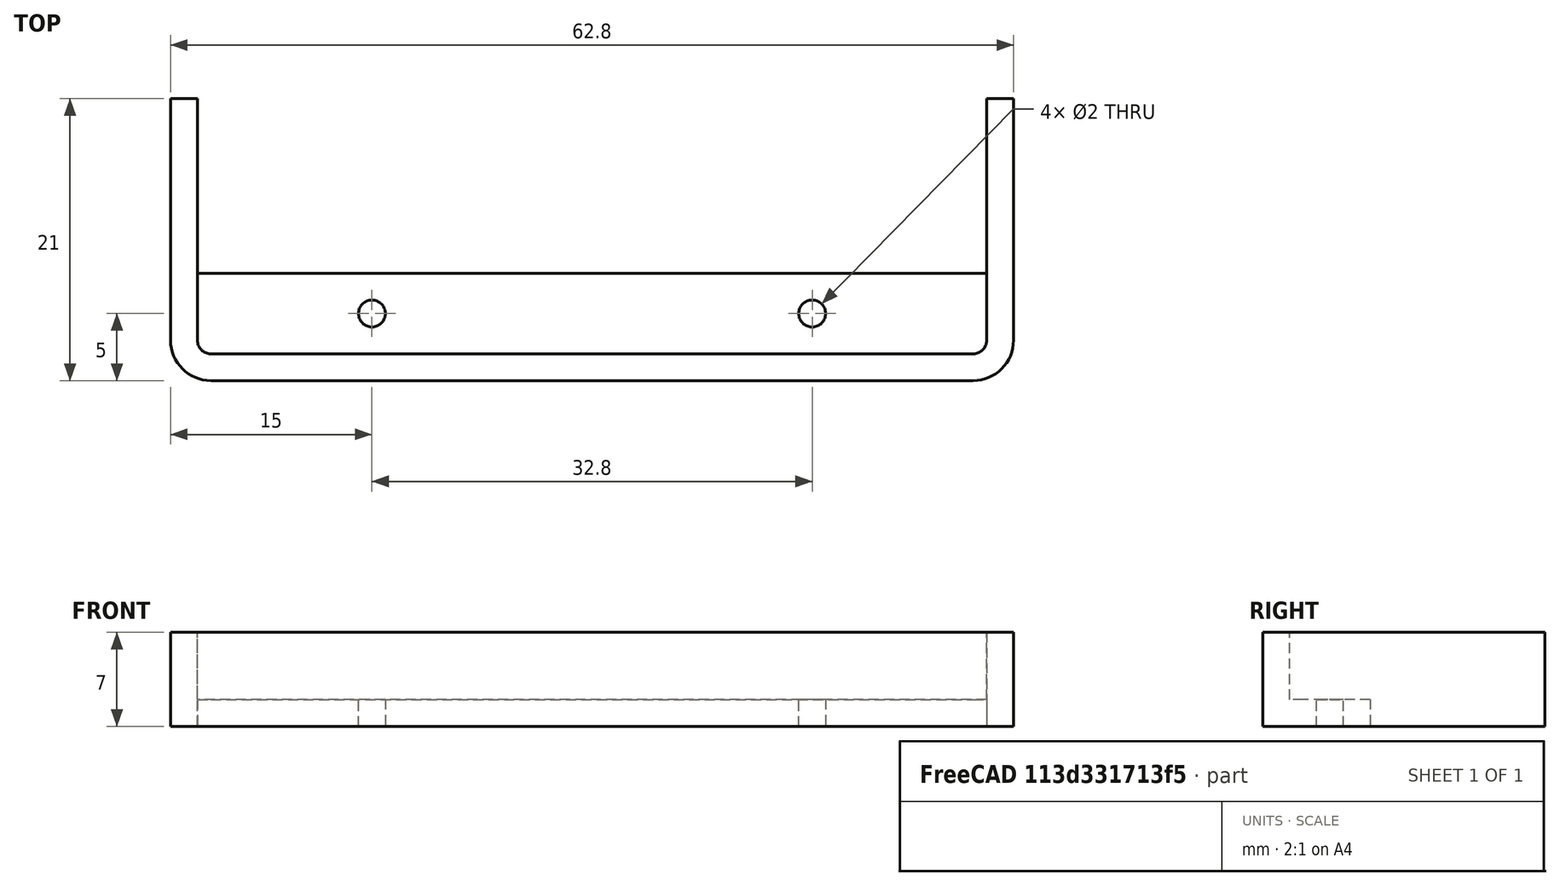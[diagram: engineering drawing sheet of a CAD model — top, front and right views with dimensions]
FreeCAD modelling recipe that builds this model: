
FCSTD DOCUMENT  (FreeCAD 0.20R28671 (Git))
Label: tapas
License: All rights reserved
LicenseURL: http://en.wikipedia.org/wiki/All_rights_reserved
objects: TechDraw::DrawViewDimension×11, Sketcher::SketchObject×4, TechDraw::DrawViewAnnotation×3, PartDesign::Pad×2, PartDesign::Pocket×2, TechDraw::DrawProjGroupItem×2, PartDesign::Fillet×1, PartDesign::Body×1, TechDraw::DrawSVGTemplate×1, Part::Refine×1, TechDraw::DrawProjGroup×1, TechDraw::DrawViewSection×1, TechDraw::DrawViewSymbol×1, TechDraw::DrawPage×1
note: 16 computed .brp shape members not serialized (recipe doc carries the construction recipe); baked Part::Feature solids carry a one-line shape summary decoded from their .brp

FEATURE [Sketcher::SketchObject] Sketch
  FullyConstrained = true
  MapMode = 5
  Support = -> [XY_Plane]
  sketch-geometry (6):
    g0: LineSegment StartX=-31.4 StartY=0 StartZ=0 EndX=31.4 EndY=0 EndZ=0
    g1: LineSegment StartX=31.4 StartY=0 StartZ=0 EndX=31.4 EndY=21 EndZ=0
    g2: LineSegment StartX=31.4 StartY=21 StartZ=0 EndX=-31.4 EndY=21 EndZ=0
    g3: LineSegment StartX=-31.4 StartY=21 StartZ=0 EndX=-31.4 EndY=0 EndZ=0
    g4: LineSegment StartX=-31.4 StartY=0 StartZ=0 EndX=0 EndY=0 EndZ=0
    g5: LineSegment StartX=0 StartY=0 StartZ=0 EndX=31.4 EndY=0 EndZ=0
  constraints (16):
    c: Coincident(g0,g1)
    c: Coincident(g1,g2)
    c: Coincident(g2,g3)
    c: Coincident(g3,g0)
    c: Horizontal(g0)
    c: Horizontal(g2)
    c: Vertical(g1)
    c: Vertical(g3)
    c: PointOnObject(g0,g-1)
    c: Coincident(g4,g0)
    c: Coincident(g5,g4)
    c: Coincident(g5,g0)
    c: Equal(g5,g4)
    c: Coincident(g4,g-1)
    c: DistanceX(g0,g0) = 62.8
    c: DistanceY(g3,g3) = 21
FEATURE [PartDesign::Pad] Pad
  Direction = (0,0,1)
  Length = 2
  Length2 = 100
  Profile = -> Sketch
  ReferenceAxis = -> Sketch [N_Axis]
  Type = 0
FEATURE [PartDesign::Fillet] Fillet
  Base = -> Pad [Edge1,Edge2]
  BaseFeature = -> Pad
  Radius = 3
  SupportTransform = false
  UseAllEdges = false
FEATURE [Sketcher::SketchObject] Sketch001
  ExternalGeometry = -> [Fillet]
  FullyConstrained = true
  MapMode = 5
  Placement = pos=(0,0,2) rot=(0,0,1;0rad)
  Support = -> [Fillet]
  sketch-geometry (4):
    g0: Circle CenterX=-16.4 CenterY=5 CenterZ=0 NormalX=0 NormalY=0 NormalZ=1 AngleXU=0 Radius=1
    g1: Circle CenterX=16.4 CenterY=5 CenterZ=0 NormalX=0 NormalY=0 NormalZ=1 AngleXU=0 Radius=1
    g2: LineSegment StartX=31.4 StartY=3 StartZ=0 EndX=16.4 EndY=3 EndZ=0
    g3: LineSegment StartX=-31.4 StartY=3 StartZ=0 EndX=-16.4 EndY=3 EndZ=0
  constraints (12):
    c: Equal(g1,g0)
    c: Horizontal(g1,g0)
    c: DistanceY(g-1,g1) = 5
    c: DistanceX(g1,g-4) = 15
    c: Coincident(g2,g-4)
    c: Horizontal(g2)
    c: Vertical(g2,g1)
    c: Coincident(g3,g-3)
    c: Horizontal(g3)
    c: Vertical(g3,g0)
    c: Equal(g3,g2)
    c: Diameter(g0) = 2
FEATURE [PartDesign::Pocket] Pocket
  BaseFeature = -> Fillet
  Direction = (0,0,-1)
  Length = 5
  Length2 = 100
  Profile = -> Sketch001
  Type = 1
FEATURE [Sketcher::SketchObject] Sketch002
  ExternalGeometry = -> [Pocket]
  FullyConstrained = true
  MapMode = 5
  Placement = pos=(0,0,2) rot=(0,0,1;0rad)
  Support = -> [Pocket]
  sketch-geometry (13):
    g0: LineSegment StartX=-31.4 StartY=21 StartZ=0 EndX=-31.4 EndY=3 EndZ=0
    g1: LineSegment StartX=-28.4 StartY=-4e-16 StartZ=0 EndX=28.4 EndY=-4e-16 EndZ=0
    g2: LineSegment StartX=31.4 StartY=3 StartZ=0 EndX=31.4 EndY=21 EndZ=0
    g3: LineSegment StartX=-31.4 StartY=21 StartZ=0 EndX=-29.4 EndY=21 EndZ=0
    g4: LineSegment StartX=-29.4 StartY=21 StartZ=0 EndX=-29.4 EndY=3 EndZ=0
    g5: LineSegment StartX=31.4 StartY=21 StartZ=0 EndX=29.4 EndY=21 EndZ=0
    g6: LineSegment StartX=29.4 StartY=21 StartZ=0 EndX=29.4 EndY=3 EndZ=0
    g7: LineSegment StartX=-28.4 StartY=2 StartZ=0 EndX=28.4 EndY=2 EndZ=0
    g8: ArcOfCircle CenterX=-28.4 CenterY=3 CenterZ=0 NormalX=0 NormalY=0 NormalZ=1 AngleXU=0 Radius=1 StartAngle=3.14159 EndAngle=4.71239
    g9: ArcOfCircle CenterX=28.4 CenterY=3 CenterZ=0 NormalX=0 NormalY=0 NormalZ=1 AngleXU=0 Radius=1 StartAngle=4.71239 EndAngle=6.28319
    g10: ArcOfCircle CenterX=-28.4 CenterY=3 CenterZ=0 NormalX=0 NormalY=0 NormalZ=1 AngleXU=0 Radius=3 StartAngle=3.14159 EndAngle=4.71239
    g11: ArcOfCircle CenterX=28.4 CenterY=3 CenterZ=0 NormalX=0 NormalY=0 NormalZ=1 AngleXU=0 Radius=3 StartAngle=4.71239 EndAngle=6.28319
    g12: LineSegment StartX=0 StartY=0 StartZ=0 EndX=0 EndY=2 EndZ=0
  constraints (30):
    c: Coincident(g0,g-3)
    c: Coincident(g0,g-6)
    c: Coincident(g1,g-6)
    c: Coincident(g1,g-5)
    c: Coincident(g2,g-5)
    c: Coincident(g2,g-4)
    c: Coincident(g3,g0)
    c: Horizontal(g3)
    c: Coincident(g4,g3)
    c: Vertical(g4)
    c: Coincident(g5,g2)
    c: Horizontal(g5)
    c: Coincident(g6,g5)
    c: Vertical(g6)
    c: Equal(g5,g3)
    c: Horizontal(g7)
    c: Tangent(g9,g7) = -1.5708
    c: Tangent(g9,g6) = 1.5708
    c: Tangent(g8,g7) = -1.5708
    c: Tangent(g8,g4) = -1.5708
    c: Coincident(g10,g0)
    c: Coincident(g11,g1)
    c: DistanceX(g0,g3) = 2
    c: Coincident(g12,g-1)
    c: PointOnObject(g12,g7)
    c: Vertical(g12)
    c: Equal(g9,g8)
    c: Coincident(g8,g10)
    c: Tangent(g10,g1) = -1.5708
    c: Tangent(g11,g2) = -1.5708
FEATURE [PartDesign::Pad] Pad001
  BaseFeature = -> Pocket
  Direction = (0,0,1)
  Length = 5
  Length2 = 100
  Profile = -> Sketch002
  ReferenceAxis = -> Sketch002 [N_Axis]
  Type = 0
FEATURE [Sketcher::SketchObject] Sketch003
  ExternalGeometry = -> [Pad001]
  FullyConstrained = true
  MapMode = 5
  Placement = pos=(0,0,2) rot=(0,0,1;0rad)
  Support = -> [Pad001]
  sketch-geometry (6):
    g0: LineSegment StartX=-29.4 StartY=21 StartZ=0 EndX=29.4 EndY=21 EndZ=0
    g1: LineSegment StartX=29.4 StartY=21 StartZ=0 EndX=29.4 EndY=8 EndZ=0
    g2: LineSegment StartX=29.4 StartY=8 StartZ=0 EndX=-29.4 EndY=8 EndZ=0
    g3: LineSegment StartX=-29.4 StartY=8 StartZ=0 EndX=-29.4 EndY=21 EndZ=0
    g4: LineSegment StartX=-16.4 StartY=5 StartZ=0 EndX=-16.4 EndY=2 EndZ=0
    g5: LineSegment StartX=-16.4 StartY=5 StartZ=0 EndX=-16.4 EndY=8 EndZ=0
  constraints (16):
    c: Coincident(g0,g1)
    c: Coincident(g1,g2)
    c: Coincident(g2,g3)
    c: Coincident(g3,g0)
    c: Horizontal(g2)
    c: Vertical(g1)
    c: Vertical(g3)
    c: Coincident(g0,g-3)
    c: Coincident(g0,g-4)
    c: Coincident(g4,g-6)
    c: PointOnObject(g4,g-5)
    c: Vertical(g4)
    c: Coincident(g5,g4)
    c: PointOnObject(g5,g2)
    c: Vertical(g5)
    c: Equal(g5,g4)
FEATURE [PartDesign::Pocket] Pocket001
  BaseFeature = -> Pad001
  Direction = (0,0,-1)
  Length = 5
  Length2 = 100
  Profile = -> Sketch003
  Type = 1
FEATURE [PartDesign::Body] Body
  Group = -> [Sketch,Pad,Fillet,Sketch001,Pocket,Sketch002,Pad001,Sketch003,Pocket001]
  Origin = -> Origin
  Tip = -> Pocket001
FEATURE [TechDraw::DrawSVGTemplate] Template003
  EditableTexts = AUTHOR_NAME=Daniel García García; DATE=13-04-2022; DN=8; DOCUMENT_TYPE=Plano de pieza; PN=11; REVISION=1; SCALE=1:1; SHEET=8/15; SIZE=A4; TITLELINE-1=Rueda de Pitch
  Height = 210
  Orientation = 1
  Width = 297
FEATURE [Part::Refine] Pocket001001
  Source = -> Pocket001
FEATURE [TechDraw::DrawProjGroupItem] ProjItem  label="Front"
  CoarseView = false
  Direction = (0,1,0)
  Focus = 100
  HardHidden = false
  IsoCount = 0
  IsoHidden = false
  IsoVisible = false
  LockPosition = true
  Perspective = false
  Rotation = 0
  RotationVector = (1,0,0)
  ScaleType = 2
  SeamHidden = false
  SeamVisible = true
  SmoothHidden = false
  SmoothVisible = true
  Source = -> [Pocket001]
  Type = 0
  X = 0
  XDirection = (1,0,0)
  Y = 0
FEATURE [TechDraw::DrawProjGroupItem] ProjItem001  label="Top"
  CoarseView = false
  Direction = (0,0,-1)
  Focus = 100
  HardHidden = false
  IsoCount = 0
  IsoHidden = false
  IsoVisible = false
  LockPosition = true
  Perspective = false
  Rotation = 0
  RotationVector = (1,0,0)
  ScaleType = 2
  SeamHidden = false
  SeamVisible = true
  SmoothHidden = false
  SmoothVisible = true
  Source = -> [Pocket001]
  Type = 4
  X = 0
  XDirection = (1,0,0)
  Y = -55.9843
FEATURE [TechDraw::DrawProjGroup] ProjGroup
  Anchor = -> ProjItem
  AutoDistribute = true
  LockPosition = true
  ProjectionType = 0
  Rotation = 0
  ScaleType = 0
  Source = -> [Pocket001]
  Views = -> [ProjItem,ProjItem001]
  X = 194.654
  Y = 140
  spacingX = 15
  spacingY = 15
FEATURE [TechDraw::DrawViewSection] SectionView  label="Section A - A"
  BaseView = -> ProjItem
  CoarseView = false
  CutSurfaceDisplay = 2
  Direction = (1,0,0)
  FileGeomPattern = <path>
  FileHatchPattern = <path>
  Focus = 100
  FuseBeforeCut = false
  HardHidden = false
  HatchScale = 1
  IsoCount = 0
  IsoHidden = false
  IsoVisible = false
  LockPosition = true
  NameGeomPattern = Diamond
  Perspective = false
  Rotation = 0
  ScaleType = 2
  SeamHidden = false
  SeamVisible = true
  SectionDirection = 1
  SectionNormal = (1,0,0)
  SectionOrigin = (-16,10.5,3.5)
  SectionSymbol = A
  SmoothHidden = false
  SmoothVisible = true
  Source = -> [Pocket001]
  X = 71.1788
  XDirection = (0,-1,0)
  Y = 140
FEATURE [TechDraw::DrawViewDimension] Dimension
  AngleOverride = false
  Arbitrary = false
  ArbitraryTolerances = false
  EqualTolerance = true
  ExtensionAngle = 0
  FormatSpec = %.2w
  FormatSpecOverTolerance = %+.2w
  FormatSpecUnderTolerance = %+.2w
  Inverted = false
  LineAngle = 0
  LockPosition = false
  MeasureType = 1
  OverTolerance = 0
  References2D = -> [ProjItem001]
  Rotation = 0
  ScaleType = 0
  TheoreticalExact = false
  Type = 1
  UnderTolerance = 0
  X = 1.65088
  Y = -12.9526
FEATURE [TechDraw::DrawViewDimension] Dimension001
  AngleOverride = false
  Arbitrary = false
  ArbitraryTolerances = false
  EqualTolerance = true
  ExtensionAngle = 0
  FormatSpec = %.2w
  FormatSpecOverTolerance = %+.2w
  FormatSpecUnderTolerance = %+.2w
  Inverted = false
  LineAngle = 0
  LockPosition = false
  MeasureType = 1
  OverTolerance = 0
  References2D = -> [ProjItem001]
  Rotation = 0
  ScaleType = 0
  TheoreticalExact = false
  Type = 2
  UnderTolerance = 0
  X = -23.0323
  Y = -1.73584
FEATURE [TechDraw::DrawViewDimension] Dimension002
  AngleOverride = false
  Arbitrary = false
  ArbitraryTolerances = false
  EqualTolerance = true
  ExtensionAngle = 0
  FormatSpec = %.2w
  FormatSpecOverTolerance = %+.2w
  FormatSpecUnderTolerance = %+.2w
  Inverted = false
  LineAngle = 0
  LockPosition = false
  MeasureType = 1
  OverTolerance = 0
  References2D = -> [ProjItem001]
  Rotation = 0
  ScaleType = 0
  TheoreticalExact = false
  Type = 2
  UnderTolerance = 0
  X = 35.796
  Y = 2.02832
FEATURE [TechDraw::DrawViewDimension] Dimension003
  AngleOverride = false
  Arbitrary = false
  ArbitraryTolerances = false
  EqualTolerance = true
  ExtensionAngle = 0
  FormatSpec = ⌀%.2w
  FormatSpecOverTolerance = %+.2w
  FormatSpecUnderTolerance = %+.2w
  Inverted = false
  LineAngle = 0
  LockPosition = false
  MeasureType = 1
  OverTolerance = 0
  References2D = -> [ProjItem001]
  Rotation = 0
  ScaleType = 0
  TheoreticalExact = false
  Type = 5
  UnderTolerance = 0
  X = -5.18848
  Y = 18.6314
FEATURE [TechDraw::DrawViewDimension] Dimension004
  AngleOverride = false
  Arbitrary = false
  ArbitraryTolerances = false
  EqualTolerance = true
  ExtensionAngle = 0
  FormatSpec = %.2w
  FormatSpecOverTolerance = %+.2w
  FormatSpecUnderTolerance = %+.2w
  Inverted = false
  LineAngle = 0
  LockPosition = false
  MeasureType = 1
  OverTolerance = 0
  References2D = -> [ProjItem001]
  Rotation = 0
  ScaleType = 0
  TheoreticalExact = false
  Type = 1
  UnderTolerance = 0
  X = 0.47168
  Y = -4.90528
FEATURE [TechDraw::DrawViewDimension] Dimension005
  AngleOverride = false
  Arbitrary = false
  ArbitraryTolerances = false
  EqualTolerance = true
  ExtensionAngle = 0
  FormatSpec = %.2w
  FormatSpecOverTolerance = %+.2w
  FormatSpecUnderTolerance = %+.2w
  Inverted = false
  LineAngle = 0
  LockPosition = false
  MeasureType = 1
  OverTolerance = 0
  References2D = -> [ProjItem001]
  Rotation = 0
  ScaleType = 0
  TheoreticalExact = false
  Type = 1
  UnderTolerance = 0
  X = 0
  Y = 9.41504
FEATURE [TechDraw::DrawViewDimension] Dimension006
  AngleOverride = false
  Arbitrary = false
  ArbitraryTolerances = false
  EqualTolerance = true
  ExtensionAngle = 0
  FormatSpec = R%.2w
  FormatSpecOverTolerance = %+.2w
  FormatSpecUnderTolerance = %+.2w
  Inverted = false
  LineAngle = 0
  LockPosition = false
  MeasureType = 1
  OverTolerance = 0
  References2D = -> [ProjItem001]
  Rotation = 0
  ScaleType = 0
  TheoreticalExact = false
  Type = 4
  UnderTolerance = 0
  X = -41.9795
  Y = 21.9331
FEATURE [TechDraw::DrawViewDimension] Dimension007
  AngleOverride = false
  Arbitrary = false
  ArbitraryTolerances = false
  EqualTolerance = true
  ExtensionAngle = 0
  FormatSpec = %.2w
  FormatSpecOverTolerance = %+.2w
  FormatSpecUnderTolerance = %+.2w
  Inverted = false
  LineAngle = 0
  LockPosition = false
  MeasureType = 1
  OverTolerance = 0
  References2D = -> [ProjItem]
  Rotation = 0
  ScaleType = 0
  TheoreticalExact = false
  Type = 2
  UnderTolerance = 0
  X = 37.8902
  Y = 7.3584
FEATURE [TechDraw::DrawViewDimension] Dimension008
  AngleOverride = false
  Arbitrary = false
  ArbitraryTolerances = false
  EqualTolerance = true
  ExtensionAngle = 0
  FormatSpec = %.2w
  FormatSpecOverTolerance = %+.2w
  FormatSpecUnderTolerance = %+.2w
  Inverted = false
  LineAngle = 0
  LockPosition = false
  MeasureType = 1
  OverTolerance = 0
  References2D = -> [SectionView]
  Rotation = 0
  ScaleType = 0
  TheoreticalExact = false
  Type = 2
  UnderTolerance = 0
  X = 26.714
  Y = 2.33622
FEATURE [TechDraw::DrawViewDimension] Dimension009
  AngleOverride = false
  Arbitrary = false
  ArbitraryTolerances = false
  EqualTolerance = true
  ExtensionAngle = 0
  FormatSpec = %.2w
  FormatSpecOverTolerance = %+.2w
  FormatSpecUnderTolerance = %+.2w
  Inverted = false
  LineAngle = 0
  LockPosition = false
  MeasureType = 1
  OverTolerance = 0
  References2D = -> [SectionView]
  Rotation = 0
  ScaleType = 0
  TheoreticalExact = false
  Type = 1
  UnderTolerance = 0
  X = 14.3625
  Y = 12.6916
FEATURE [TechDraw::DrawViewDimension] Dimension010
  AngleOverride = false
  Arbitrary = false
  ArbitraryTolerances = false
  EqualTolerance = true
  ExtensionAngle = 0
  FormatSpec = %.2w
  FormatSpecOverTolerance = %+.2w
  FormatSpecUnderTolerance = %+.2w
  Inverted = false
  LineAngle = 0
  LockPosition = false
  MeasureType = 1
  OverTolerance = 0
  References2D = -> [ProjItem]
  Rotation = 0
  ScaleType = 0
  TheoreticalExact = false
  Type = 1
  UnderTolerance = 0
  X = 33.9376
  Y = -7.09253
FEATURE [TechDraw::DrawViewAnnotation] Annotation
  Font = osifont
  LineSpace = 80
  LockPosition = false
  MaxWidth = -1
  Rotation = 0
  ScaleType = 0
  Text = Default Text
  TextSize = 5
  TextStyle = 0
  X = 148.5
  Y = 105
FEATURE [TechDraw::DrawViewSymbol] Symbol
  LockPosition = false
  Rotation = 0
  Scale = 0.3
  ScaleType = 2
  Symbol = <blob: 2444 chars omitted>
  X = 217.487
  Y = 36.9001
FEATURE [TechDraw::DrawViewAnnotation] Annotation001
  Font = osifont
  LineSpace = 80
  LockPosition = false
  MaxWidth = -1
  Rotation = 0
  ScaleType = 0
  Text = Sección A-A'
  TextSize = 5
  TextStyle = 0
  X = 73.0536
  Y = 159.464
FEATURE [TechDraw::DrawViewAnnotation] Annotation002
  Font = osifont
  LineSpace = 80
  LockPosition = false
  MaxWidth = -1
  Rotation = 0
  ScaleType = 0
  Text = '
  TextSize = 5
  TextStyle = 0
  X = 180.794
  Y = 117.702
FEATURE [TechDraw::DrawPage] Page003  label="Tapas"
  KeepUpdated = true
  NextBalloonIndex = 1
  ProjectionType = 0
  Template = -> Template003
  Views = -> [ProjGroup,SectionView,Dimension,Dimension001,Dimension002,Dimension003,Dimension004,Dimension005,Dimension006,Dimension007,Dimension008,Dimension009,Dimension010,Symbol,Annotation001,Annotation002]
note: 2 file-system paths scrubbed to <path> (originals preserved in the JSON sidecar)
